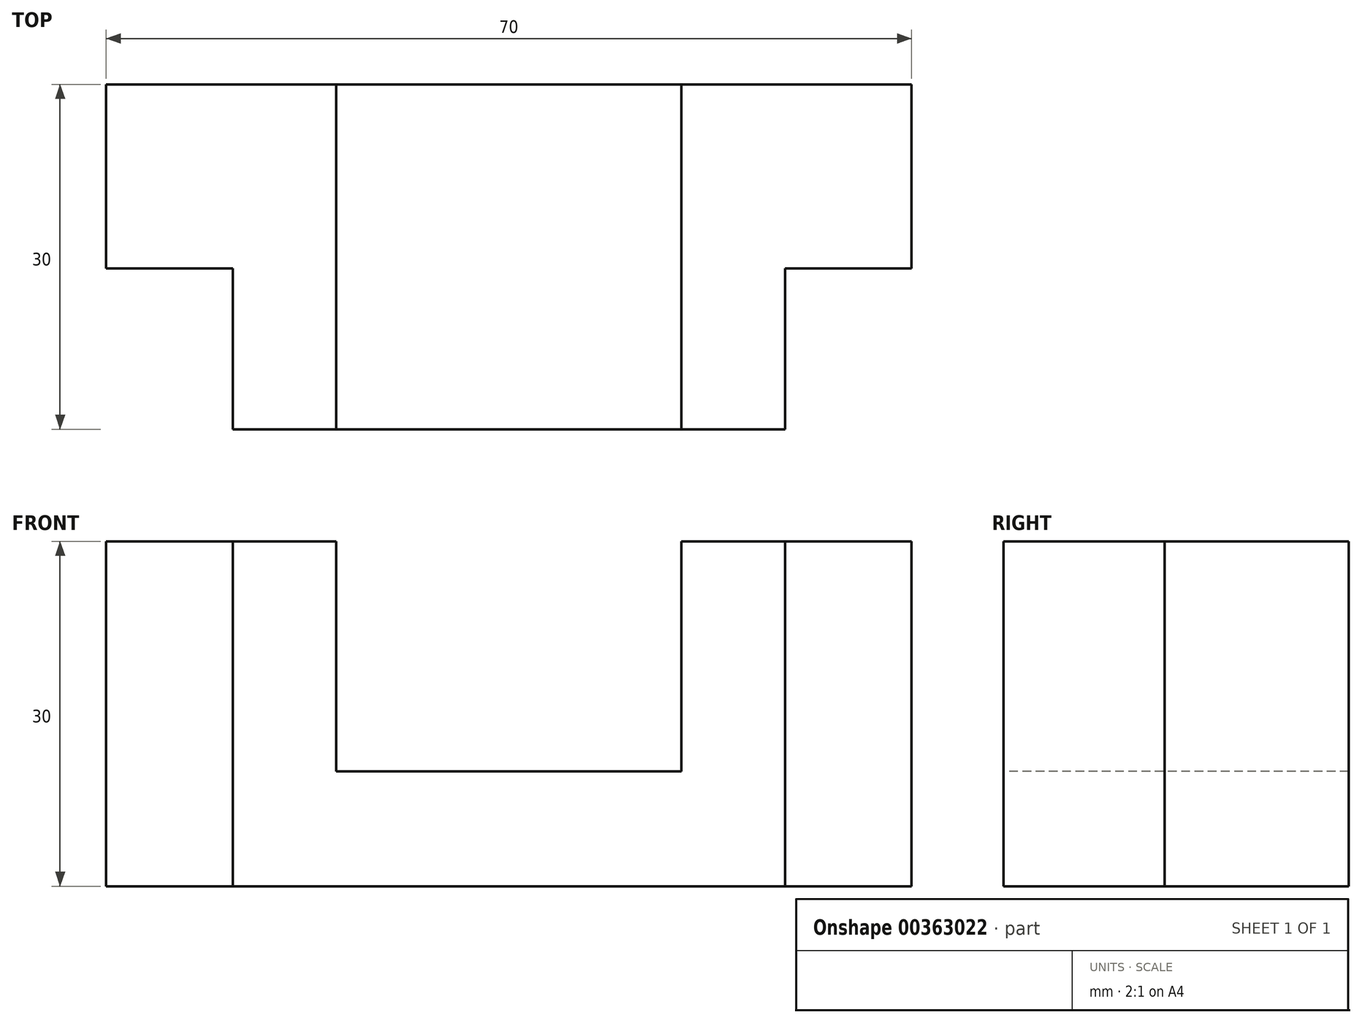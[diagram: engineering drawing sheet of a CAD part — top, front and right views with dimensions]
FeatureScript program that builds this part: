
annotation { "Feature Type Name" : "Feature", "Feature Type Description" : "" }
export const myFeature = defineFeature(function(context is Context, id is Id, definition is map)
    precondition{}
    {
        {
            var Q0;
            Q0=qCreatedBy(makeId("Top.planeOp"),FACE);
            var sketch = newSketch(context, id + "F0", { "sketchPlane" : qUnion([Q0])});
            skLineSegment(sketch, "E0.bottom", {"start": v(24, 0) * mm, "end": v(-24, 0) * mm});
            skLineSegment(sketch, "E0.top", {"start": v(35, 30) * mm, "end": v(-35, 30) * mm});
            skLineSegment(sketch, "E0.left", {"start": v(35, 14) * mm, "end": v(35, 30) * mm});
            skLineSegment(sketch, "E0.right", {"start": v(-35, 14) * mm, "end": v(-35, 30) * mm});
            skLineSegment(sketch, "E1.bottom", {"start": v(-15, 0) * mm, "end": v(15, 0) * mm});
            skLineSegment(sketch, "E1.top", {"start": v(-15, 30) * mm, "end": v(15, 30) * mm});
            skLineSegment(sketch, "E2.bottom", {"start": v(-24, 0) * mm, "end": v(15, 0) * mm});
            skLineSegment(sketch, "E2.left", {"start": v(-24, 0) * mm, "end": v(-24, 14) * mm});
            skLineSegment(sketch, "E2.right", {"start": v(24, 0) * mm, "end": v(24, 14) * mm});
            skLineSegment(sketch, "E3.bottom", {"start": v(-24, 14) * mm, "end": v(-35, 14) * mm});
            skLineSegment(sketch, "E3.top", {"start": v(-24, 14) * mm, "end": v(-35, 14) * mm});
            skLineSegment(sketch, "E3.left", {"start": v(-24, 14) * mm, "end": v(-24, 14) * mm});
            skLineSegment(sketch, "E3.right", {"start": v(-35, 14) * mm, "end": v(-35, 14) * mm});
            skLineSegment(sketch, "E4.bottom", {"start": v(24, 14) * mm, "end": v(35, 14) * mm});
            skLineSegment(sketch, "E4.top", {"start": v(24, 14) * mm, "end": v(35, 14) * mm});
            skLineSegment(sketch, "E4.left", {"start": v(24, 14) * mm, "end": v(24, 14) * mm});
            skLineSegment(sketch, "E4.right", {"start": v(35, 14) * mm, "end": v(35, 14) * mm});
            skPoint(sketch, "E5.orphan", {"position": v(-35, 0) * mm});
            skPoint(sketch, "E6.orphan", {"position": v(35, 0) * mm});
            skSolve(sketch);
        }
        {
            var Q0;
            {var subQ2=sQuery(id+"F0.wireOp",EDGE,"E0.bottom");Q0=makeQuery(id+"F0.imprint","IMPRINT",FACE,{"disambiguationData":[TD([[makeQuery(id+"F0.imprint","IMPRINT",EDGE,{"derivedFrom":subQ2}),-1.0]])]});}
            extrude(context, id + "F1", {"entities" : qUnion([Q0]), "depth" : 30 * mm});
        }
        {
            var Q0;
            Q0=makeQuery(id+"F1.opExtrude","SWEPT_FACE",FACE,{"disambiguationData":[OSD([sQuery(id+"F0.wireOp",EDGE,"E0.bottom"),sQuery(id+"F0.wireOp",EDGE,"E2.bottom")])]});
            var sketch = newSketch(context, id + "F2", { "sketchPlane" : qUnion([Q0])});
            skLineSegment(sketch, "E7.bottom", {"start": v(-15, 35) * mm, "end": v(15, 35) * mm});
            skLineSegment(sketch, "E7.top", {"start": v(-15, 10) * mm, "end": v(15, 10) * mm});
            skLineSegment(sketch, "E7.left", {"start": v(-15, 35) * mm, "end": v(-15, 10) * mm});
            skLineSegment(sketch, "E7.right", {"start": v(15, 35) * mm, "end": v(15, 10) * mm});
            skSolve(sketch);
        }
        {
            var Q0;
            {var subQ0=sQuery(id+"F2.wireOp",EDGE,"E7.top");Q0=makeQuery(id+"F2.imprint","IMPRINT",FACE,{"disambiguationData":[TD([[makeQuery(id+"F2.imprint","IMPRINT",EDGE,{"derivedFrom":subQ0}),1.0]])]});}
            extrude(context, id + "F3", {"entities" : qUnion([Q0]), "operationType" : NewBodyOperationType.REMOVE, "oppositeDirection" : true, "depth" : 30 * mm});
        }
    });
